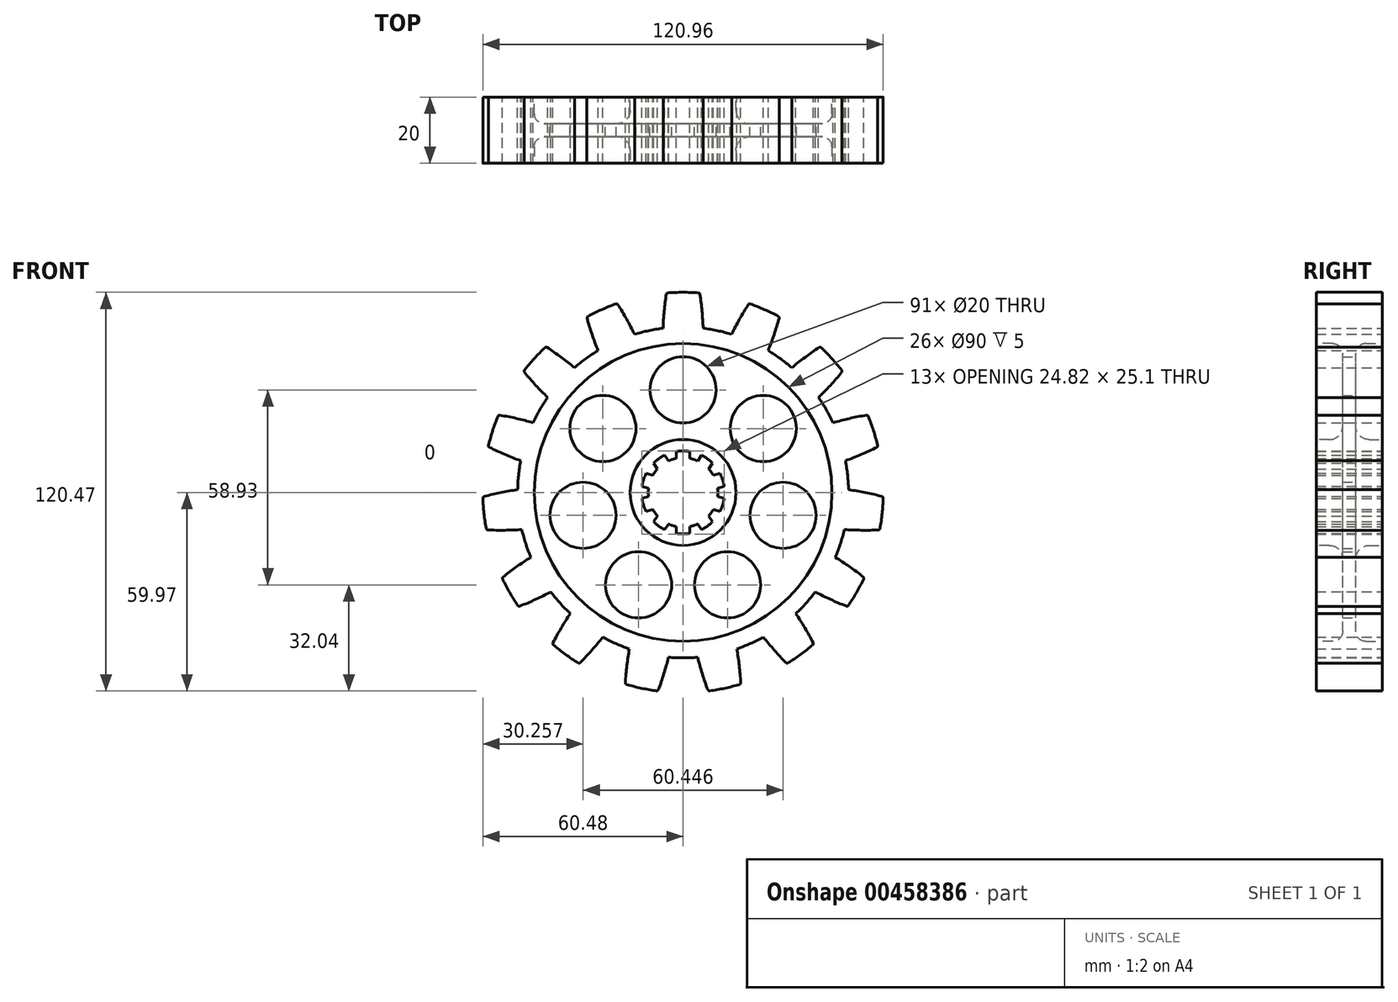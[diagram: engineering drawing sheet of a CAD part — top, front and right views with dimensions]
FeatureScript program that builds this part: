
annotation { "Feature Type Name" : "Feature", "Feature Type Description" : "" }
export const myFeature = defineFeature(function(context is Context, id is Id, definition is map)
    precondition{}
    {
        {
            var Q0;
            Q0=qCreatedBy(makeId("Front.planeOp"),FACE);
            var sketch = newSketch(context, id + "F0", { "sketchPlane" : qUnion([Q0])});
            skCircle(sketch, "E0", {"center": v(0, 0) * mm, "radius": 50 * mm});
            skArc(sketch, "E1", {"start": v(-60.49, -1.3) * mm, "mid": v(-60.17, -6.32) * mm, "end": v(-59.43, -11.31) * mm});
            skLineSegment(sketch, "E2.0", {"start": v(0, 46.5) * mm, "end": v(-83.9, 46.5) * mm, "construction": true});
            skLineSegment(sketch, "E3", {"start": v(0, 46.5) * mm, "end": v(83.9, 46.5) * mm, "construction": true});
            skArc(sketch, "E4.trimOffspring", {"start": v(-5.04, 60.29) * mm, "mid": v(-5.7, 54.98) * mm, "end": v(-6.05, 49.63) * mm});
            skArc(sketch, "E5.1.0", {"start": v(-29.12, 53.03) * mm, "mid": v(-27.57, 47.9) * mm, "end": v(-25.71, 42.88) * mm});
            skArc(sketch, "E5.1.1", {"start": v(-14.66, 47.8) * mm, "mid": v(-17.15, 52.54) * mm, "end": v(-19.92, 57.13) * mm});
            skArc(sketch, "E5.2.1", {"start": v(-32.84, 37.7) * mm, "mid": v(-37.04, 41.02) * mm, "end": v(-41.43, 44.09) * mm});
            skArc(sketch, "E5.3.0", {"start": v(-58.9, 13.84) * mm, "mid": v(-54.05, 11.57) * mm, "end": v(-49.07, 9.59) * mm});
            skArc(sketch, "E5.3.1", {"start": v(-45.34, 21.09) * mm, "mid": v(-50.52, 22.4) * mm, "end": v(-55.78, 23.42) * mm});
            skArc(sketch, "E5.4.0", {"start": v(-59.43, -11.31) * mm, "mid": v(-54.08, -11.42) * mm, "end": v(-48.73, -11.2) * mm});
            skArc(sketch, "E5.4.1", {"start": v(-50, 0.82) * mm, "mid": v(-55.27, -0.08) * mm, "end": v(-60.49, -1.3) * mm});
            skArc(sketch, "E5.5.0", {"start": v(-49.7, -34.5) * mm, "mid": v(-44.76, -32.42) * mm, "end": v(-39.96, -30.05) * mm});
            skArc(sketch, "E5.5.1", {"start": v(-46, -19.58) * mm, "mid": v(-50.46, -22.55) * mm, "end": v(-54.73, -25.78) * mm});
            skArc(sketch, "E5.6.0", {"start": v(-31.36, -51.74) * mm, "mid": v(-27.7, -47.83) * mm, "end": v(-24.28, -43.7) * mm});
            skArc(sketch, "E5.6.1", {"start": v(-34.06, -36.6) * mm, "mid": v(-36.93, -41.13) * mm, "end": v(-39.51, -45.81) * mm});
            skArc(sketch, "E5.7.0", {"start": v(-7.6, -60.02) * mm, "mid": v(-5.85, -54.96) * mm, "end": v(-4.4, -49.8) * mm});
            skArc(sketch, "E5.7.1", {"start": v(-16.23, -47.3) * mm, "mid": v(-17, -52.6) * mm, "end": v(-17.46, -57.93) * mm});
            skArc(sketch, "E5.8.0", {"start": v(17.46, -57.93) * mm, "mid": v(17, -52.6) * mm, "end": v(16.23, -47.3) * mm});
            skArc(sketch, "E5.8.1", {"start": v(4.4, -49.8) * mm, "mid": v(5.85, -54.96) * mm, "end": v(7.6, -60.02) * mm});
            skArc(sketch, "E5.9.0", {"start": v(39.51, -45.81) * mm, "mid": v(36.93, -41.13) * mm, "end": v(34.06, -36.6) * mm});
            skArc(sketch, "E5.9.1", {"start": v(24.28, -43.7) * mm, "mid": v(27.7, -47.83) * mm, "end": v(31.36, -51.74) * mm});
            skArc(sketch, "E5.10.0", {"start": v(54.73, -25.78) * mm, "mid": v(50.46, -22.55) * mm, "end": v(46, -19.58) * mm});
            skArc(sketch, "E5.10.1", {"start": v(39.96, -30.05) * mm, "mid": v(44.76, -32.42) * mm, "end": v(49.7, -34.5) * mm});
            skArc(sketch, "E5.11.0", {"start": v(60.49, -1.3) * mm, "mid": v(55.27, -0.08) * mm, "end": v(50, 0.82) * mm});
            skArc(sketch, "E5.11.1", {"start": v(48.73, -11.2) * mm, "mid": v(54.08, -11.42) * mm, "end": v(59.43, -11.31) * mm});
            skArc(sketch, "E5.12.0", {"start": v(55.78, 23.42) * mm, "mid": v(50.52, 22.4) * mm, "end": v(45.34, 21.09) * mm});
            skArc(sketch, "E5.12.1", {"start": v(49.07, 9.59) * mm, "mid": v(54.05, 11.57) * mm, "end": v(58.9, 13.84) * mm});
            skArc(sketch, "E5.13.0", {"start": v(41.43, 44.09) * mm, "mid": v(37.04, 41.02) * mm, "end": v(32.84, 37.7) * mm});
            skArc(sketch, "E5.13.1", {"start": v(40.93, 28.72) * mm, "mid": v(44.67, 32.55) * mm, "end": v(48.17, 36.6) * mm});
            skArc(sketch, "E5.14.0", {"start": v(19.92, 57.13) * mm, "mid": v(17.15, 52.54) * mm, "end": v(14.66, 47.8) * mm});
            skArc(sketch, "E5.14.1", {"start": v(25.71, 42.88) * mm, "mid": v(27.57, 47.9) * mm, "end": v(29.12, 53.03) * mm});
            skArc(sketch, "E6.trimOffspring", {"start": v(6.05, 49.63) * mm, "mid": v(5.7, 54.98) * mm, "end": v(5.04, 60.29) * mm});
            skArc(sketch, "E7.trimOffspring", {"start": v(-48.17, 36.6) * mm, "mid": v(-44.67, 32.55) * mm, "end": v(-40.93, 28.72) * mm});
            skCircle(sketch, "E8", {"center": v(0, 0) * mm, "radius": 10.5 * mm});
            skArc(sketch, "E9", {"start": v(8.94, 8.81) * mm, "mid": v(7.38, 10.15) * mm, "end": v(5.62, 11.22) * mm});
            skLineSegment(sketch, "E10.0", {"start": v(-2.05, -10.3) * mm, "end": v(-2.05, 12.38) * mm});
            skLineSegment(sketch, "E11.2.1", {"start": v(11.14, -5.78) * mm, "end": v(-12.4, 1.88) * mm});
            skLineSegment(sketch, "E11.4.1", {"start": v(8.94, 8.81) * mm, "end": v(-5.62, -11.22) * mm});
            skLineSegment(sketch, "E11.4.2", {"start": v(4.4, 9.54) * mm, "end": v(-8.94, -8.81) * mm});
            skLineSegment(sketch, "E11.5.2", {"start": v(-2.05, 12.38) * mm, "end": v(-2.05, -12.38) * mm});
            skLineSegment(sketch, "E11.6.2", {"start": v(-8.94, 8.81) * mm, "end": v(5.62, -11.22) * mm});
            skLineSegment(sketch, "E12.trimOffspring", {"start": v(-5.62, 11.22) * mm, "end": v(8.94, -8.81) * mm});
            skLineSegment(sketch, "E13.trimOffspring", {"start": v(2.05, 12.38) * mm, "end": v(2.05, -12.38) * mm});
            skLineSegment(sketch, "E14.trimOffspring", {"start": v(-11.14, 5.78) * mm, "end": v(12.4, -1.88) * mm});
            skLineSegment(sketch, "E15.trimOffspring", {"start": v(-12.4, 1.88) * mm, "end": v(11.14, -5.78) * mm});
            skLineSegment(sketch, "E16.trimOffspring", {"start": v(12.4, 1.88) * mm, "end": v(-11.14, -5.78) * mm});
            skLineSegment(sketch, "E17.trimOffspring", {"start": v(11.14, 5.78) * mm, "end": v(-12.4, -1.88) * mm});
            skLineSegment(sketch, "E18.trimOffspring", {"start": v(12.4, -1.88) * mm, "end": v(-11.14, 5.78) * mm});
            skLineSegment(sketch, "E19.trimOffspring", {"start": v(8.94, -8.81) * mm, "end": v(-5.62, 11.22) * mm});
            skLineSegment(sketch, "E20.trimOffspring", {"start": v(5.62, -11.22) * mm, "end": v(-8.94, 8.81) * mm});
            skLineSegment(sketch, "E21.trimOffspring", {"start": v(2.05, -12.38) * mm, "end": v(2.05, 12.38) * mm});
            skLineSegment(sketch, "E22.trimOffspring", {"start": v(-5.62, -11.22) * mm, "end": v(8.94, 8.81) * mm});
            skLineSegment(sketch, "E23.trimOffspring", {"start": v(-8.94, -8.81) * mm, "end": v(5.62, 11.22) * mm});
            skLineSegment(sketch, "E24.trimOffspring", {"start": v(-12.4, -1.88) * mm, "end": v(9.16, 5.13) * mm});
            skLineSegment(sketch, "E25.trimOffspring", {"start": v(-11.14, -5.78) * mm, "end": v(12.4, 1.88) * mm});
            skArc(sketch, "E26.trimOffspring", {"start": v(12.4, 1.88) * mm, "mid": v(11.94, 3.88) * mm, "end": v(11.14, 5.78) * mm});
            skArc(sketch, "E27.trimOffspring", {"start": v(11.14, -5.78) * mm, "mid": v(11.94, -3.88) * mm, "end": v(12.4, -1.88) * mm});
            skArc(sketch, "E28.trimOffspring", {"start": v(5.62, -11.22) * mm, "mid": v(7.38, -10.15) * mm, "end": v(8.94, -8.81) * mm});
            skArc(sketch, "E29.trimOffspring", {"start": v(-2.05, -12.38) * mm, "mid": v(0, -12.55) * mm, "end": v(2.05, -12.38) * mm});
            skArc(sketch, "E30.trimOffspring", {"start": v(-8.94, -8.81) * mm, "mid": v(-7.38, -10.15) * mm, "end": v(-5.62, -11.22) * mm});
            skArc(sketch, "E31.trimOffspring", {"start": v(-12.4, -1.88) * mm, "mid": v(-11.94, -3.88) * mm, "end": v(-11.14, -5.78) * mm});
            skArc(sketch, "E32.trimOffspring", {"start": v(-11.14, 5.78) * mm, "mid": v(-11.94, 3.88) * mm, "end": v(-12.4, 1.88) * mm});
            skArc(sketch, "E33.trimOffspring", {"start": v(-5.62, 11.22) * mm, "mid": v(-7.38, 10.15) * mm, "end": v(-8.94, 8.81) * mm});
            skArc(sketch, "E34.trimOffspring", {"start": v(2.05, 12.38) * mm, "mid": v(0, 12.55) * mm, "end": v(-2.05, 12.38) * mm});
            skArc(sketch, "E35.trimOffspring", {"start": v(-55.78, 23.42) * mm, "mid": v(-57.54, 18.7) * mm, "end": v(-58.9, 13.84) * mm});
            skArc(sketch, "E36.trimOffspring", {"start": v(-41.43, 44.09) * mm, "mid": v(-44.96, 40.48) * mm, "end": v(-48.17, 36.6) * mm});
            skArc(sketch, "E37.trimOffspring", {"start": v(-19.92, 57.13) * mm, "mid": v(-24.6, 55.27) * mm, "end": v(-29.12, 53.03) * mm});
            skArc(sketch, "E38.trimOffspring", {"start": v(5.04, 60.29) * mm, "mid": v(0, 60.5) * mm, "end": v(-5.04, 60.29) * mm});
            skArc(sketch, "E39.trimOffspring", {"start": v(29.12, 53.03) * mm, "mid": v(24.6, 55.27) * mm, "end": v(19.92, 57.13) * mm});
            skArc(sketch, "E40.trimOffspring", {"start": v(48.17, 36.6) * mm, "mid": v(44.96, 40.48) * mm, "end": v(41.43, 44.09) * mm});
            skArc(sketch, "E41.trimOffspring", {"start": v(58.9, 13.84) * mm, "mid": v(57.54, 18.7) * mm, "end": v(55.78, 23.42) * mm});
            skArc(sketch, "E42.trimOffspring", {"start": v(59.43, -11.31) * mm, "mid": v(60.17, -6.32) * mm, "end": v(60.49, -1.3) * mm});
            skArc(sketch, "E43.trimOffspring", {"start": v(49.7, -34.5) * mm, "mid": v(52.4, -30.25) * mm, "end": v(54.73, -25.78) * mm});
            skArc(sketch, "E44.trimOffspring", {"start": v(31.36, -51.74) * mm, "mid": v(35.56, -48.95) * mm, "end": v(39.51, -45.81) * mm});
            skArc(sketch, "E45.trimOffspring", {"start": v(7.6, -60.02) * mm, "mid": v(12.58, -59.18) * mm, "end": v(17.46, -57.93) * mm});
            skArc(sketch, "E46.trimOffspring", {"start": v(-17.46, -57.93) * mm, "mid": v(-12.58, -59.18) * mm, "end": v(-7.6, -60.02) * mm});
            skArc(sketch, "E47.trimOffspring", {"start": v(-39.51, -45.81) * mm, "mid": v(-35.56, -48.95) * mm, "end": v(-31.36, -51.74) * mm});
            skArc(sketch, "E48.trimOffspring", {"start": v(-54.73, -25.78) * mm, "mid": v(-52.4, -30.25) * mm, "end": v(-49.7, -34.5) * mm});
            skSolve(sketch);
        }
        {
            var Q0;
            {var subQ9=sQuery(id+"F0.wireOp",EDGE,"E9");Q0=makeQuery(id+"F0.imprint","IMPRINT",FACE,{"disambiguationData":[TD([[makeQuery(id+"F0.imprint","IMPRINT",EDGE,{"derivedFrom":subQ9}),-1.0]])]});}
            var Q1;
            Q1=makeQuery(id+"F0.imprint","IMPRINT",FACE,{"disambiguationData":[TD([[makeQuery(id+"F0.imprint","IMPRINT",EDGE,{"derivedFrom":sQuery(id+"F0.wireOp",EDGE,"E1")}),1.0]])]});
            var Q2;
            {var subQ0=sQuery(id+"F0.wireOp",EDGE,"E5.3.0");Q2=makeQuery(id+"F0.imprint","IMPRINT",FACE,{"disambiguationData":[TD([[makeQuery(id+"F0.imprint","IMPRINT",EDGE,{"derivedFrom":subQ0}),1.0]])]});}
            var Q3;
            {var subQ0=sQuery(id+"F0.wireOp",EDGE,"E5.2.1");Q3=makeQuery(id+"F0.imprint","IMPRINT",FACE,{"disambiguationData":[TD([[makeQuery(id+"F0.imprint","IMPRINT",EDGE,{"derivedFrom":subQ0}),1.0]])]});}
            var Q4;
            {var subQ0=sQuery(id+"F0.wireOp",EDGE,"E5.1.0");Q4=makeQuery(id+"F0.imprint","IMPRINT",FACE,{"disambiguationData":[TD([[makeQuery(id+"F0.imprint","IMPRINT",EDGE,{"derivedFrom":subQ0}),1.0]])]});}
            var Q5;
            {var subQ0=sQuery(id+"F0.wireOp",EDGE,"E4.trimOffspring");Q5=makeQuery(id+"F0.imprint","IMPRINT",FACE,{"disambiguationData":[TD([[makeQuery(id+"F0.imprint","IMPRINT",EDGE,{"derivedFrom":subQ0}),1.0]])]});}
            var Q6;
            {var subQ0=sQuery(id+"F0.wireOp",EDGE,"E5.14.0");Q6=makeQuery(id+"F0.imprint","IMPRINT",FACE,{"disambiguationData":[TD([[makeQuery(id+"F0.imprint","IMPRINT",EDGE,{"derivedFrom":subQ0}),1.0]])]});}
            var Q7;
            {var subQ0=sQuery(id+"F0.wireOp",EDGE,"E5.13.0");Q7=makeQuery(id+"F0.imprint","IMPRINT",FACE,{"disambiguationData":[TD([[makeQuery(id+"F0.imprint","IMPRINT",EDGE,{"derivedFrom":subQ0}),1.0]])]});}
            var Q8;
            {var subQ0=sQuery(id+"F0.wireOp",EDGE,"E5.12.0");Q8=makeQuery(id+"F0.imprint","IMPRINT",FACE,{"disambiguationData":[TD([[makeQuery(id+"F0.imprint","IMPRINT",EDGE,{"derivedFrom":subQ0}),1.0]])]});}
            var Q9;
            {var subQ0=sQuery(id+"F0.wireOp",EDGE,"E5.11.0");Q9=makeQuery(id+"F0.imprint","IMPRINT",FACE,{"disambiguationData":[TD([[makeQuery(id+"F0.imprint","IMPRINT",EDGE,{"derivedFrom":subQ0}),1.0]])]});}
            var Q10;
            {var subQ0=sQuery(id+"F0.wireOp",EDGE,"E5.10.0");Q10=makeQuery(id+"F0.imprint","IMPRINT",FACE,{"disambiguationData":[TD([[makeQuery(id+"F0.imprint","IMPRINT",EDGE,{"derivedFrom":subQ0}),1.0]])]});}
            var Q11;
            {var subQ0=sQuery(id+"F0.wireOp",EDGE,"E5.9.0");Q11=makeQuery(id+"F0.imprint","IMPRINT",FACE,{"disambiguationData":[TD([[makeQuery(id+"F0.imprint","IMPRINT",EDGE,{"derivedFrom":subQ0}),1.0]])]});}
            var Q12;
            {var subQ0=sQuery(id+"F0.wireOp",EDGE,"E5.8.0");Q12=makeQuery(id+"F0.imprint","IMPRINT",FACE,{"disambiguationData":[TD([[makeQuery(id+"F0.imprint","IMPRINT",EDGE,{"derivedFrom":subQ0}),1.0]])]});}
            var Q13;
            {var subQ0=sQuery(id+"F0.wireOp",EDGE,"E5.7.0");Q13=makeQuery(id+"F0.imprint","IMPRINT",FACE,{"disambiguationData":[TD([[makeQuery(id+"F0.imprint","IMPRINT",EDGE,{"derivedFrom":subQ0}),1.0]])]});}
            var Q14;
            {var subQ0=sQuery(id+"F0.wireOp",EDGE,"E5.6.0");Q14=makeQuery(id+"F0.imprint","IMPRINT",FACE,{"disambiguationData":[TD([[makeQuery(id+"F0.imprint","IMPRINT",EDGE,{"derivedFrom":subQ0}),1.0]])]});}
            var Q15;
            {var subQ0=sQuery(id+"F0.wireOp",EDGE,"E5.5.0");Q15=makeQuery(id+"F0.imprint","IMPRINT",FACE,{"disambiguationData":[TD([[makeQuery(id+"F0.imprint","IMPRINT",EDGE,{"derivedFrom":subQ0}),1.0]])]});}
            extrude(context, id + "F1", {"entities" : qUnion([Q0, Q1, Q2, Q3, Q4, Q5, Q6, Q7, Q8, Q9, Q10, Q11, Q12, Q13, Q14, Q15]), "depth" : 20 * mm, "offsetDistance" : 25 * mm});
        }
        {
            var Q0;
            Q0=qCreatedBy(makeId("Front.planeOp"),FACE);
            var sketch = newSketch(context, id + "F2", { "sketchPlane" : qUnion([Q0])});
            skCircle(sketch, "E49", {"center": v(0, 31) * mm, "radius": 10 * mm});
            skCircle(sketch, "E50.1.0", {"center": v(-24.24, 19.33) * mm, "radius": 10 * mm});
            skCircle(sketch, "E50.2.0", {"center": v(-30.22, -6.9) * mm, "radius": 10 * mm});
            skCircle(sketch, "E50.3.0", {"center": v(-13.45, -27.93) * mm, "radius": 10 * mm});
            skCircle(sketch, "E50.4.0", {"center": v(13.45, -27.93) * mm, "radius": 10 * mm});
            skCircle(sketch, "E50.5.0", {"center": v(30.22, -6.9) * mm, "radius": 10 * mm});
            skCircle(sketch, "E50.6.0", {"center": v(24.24, 19.33) * mm, "radius": 10 * mm});
            skPoint(sketch, "E50.center", {"position": v(0, 0) * mm});
            skSolve(sketch);
        }
        {
            var Q0;
            Q0 = qSketchRegion(id + "F2", true);
            extrude(context, id + "F3", {"entities" : qUnion([Q0]), "operationType" : NewBodyOperationType.REMOVE, "depth" : 56 * mm, "offsetDistance" : 25 * mm});
        }
        {
            var Q0;
            Q0=qCreatedBy(makeId("Front.planeOp"),FACE);
            cPlane(context, id + "F4", {"entities" : qUnion([Q0]), "cplaneType" : CPlaneType.OFFSET, "offset" : 20 * mm, "width" : 150 * mm, "height" : 150 * mm});
        }
        {
            var Q0;
            Q0=qCreatedBy(id+"F4.planeOp",FACE);
            var sketch = newSketch(context, id + "F5", { "sketchPlane" : qUnion([Q0])});
            skCircle(sketch, "E51", {"center": v(0, 0) * mm, "radius": 16 * mm});
            skCircle(sketch, "E52", {"center": v(0, 0) * mm, "radius": 45 * mm});
            skSolve(sketch);
        }
        {
            var Q0;
            Q0=makeQuery(id+"F5.imprint","IMPRINT",FACE,{"disambiguationData":[TD([[makeQuery(id+"F5.imprint","IMPRINT",EDGE,{"derivedFrom":sQuery(id+"F5.wireOp",EDGE,"E51")}),-1.0]])]});
            extrude(context, id + "F6", {"entities" : qUnion([Q0]), "operationType" : NewBodyOperationType.REMOVE, "oppositeDirection" : true, "depth" : 8 * mm, "offsetDistance" : 25 * mm});
        }
        {
            var Q0;
            Q0=qCreatedBy(makeId("Front.planeOp"),FACE);
            var sketch = newSketch(context, id + "F7", { "sketchPlane" : qUnion([Q0])});
            skCircle(sketch, "E53", {"center": v(0, 0) * mm, "radius": 16 * mm});
            skCircle(sketch, "E54", {"center": v(0, 0) * mm, "radius": 45 * mm});
            skSolve(sketch);
        }
        {
            var Q0;
            Q0=makeQuery(id+"F7.imprint","IMPRINT",FACE,{"disambiguationData":[TD([[makeQuery(id+"F7.imprint","IMPRINT",EDGE,{"derivedFrom":sQuery(id+"F7.wireOp",EDGE,"E53")}),-1.0]])]});
            extrude(context, id + "F8", {"entities" : qUnion([Q0]), "operationType" : NewBodyOperationType.REMOVE, "depth" : 8 * mm, "offsetDistance" : 25 * mm});
        }
        {
            var Q0;
            Q0=makeQuery(id+"F6.boolean.opBoolean","COPY",EDGE,{"derivedFrom":makeQuery(id+"F6.opExtrude","CAP_EDGE",EDGE,{"disambiguationData":[OSD([sQuery(id+"F5.wireOp",EDGE,"E52")])],"isStart":false})});
            var Q1;
            Q1=makeQuery(id+"F8.boolean.opBoolean","COPY",EDGE,{"derivedFrom":makeQuery(id+"F8.opExtrude","CAP_EDGE",EDGE,{"disambiguationData":[OSD([sQuery(id+"F7.wireOp",EDGE,"E54")])],"isStart":false})});
            fillet(context, id + "F9", {"entities" : qUnion([Q0, Q1]), "radius" : 3 * mm, "tangentPropagation" : true, "allowEdgeOverflow" : false});
        }
        {
            var Q0;
            Q0=makeQuery(id+"F6.boolean.opBoolean","COPY",EDGE,{"derivedFrom":makeQuery(id+"F6.opExtrude","CAP_EDGE",EDGE,{"disambiguationData":[OSD([sQuery(id+"F5.wireOp",EDGE,"E51")])],"isStart":false})});
            var Q1;
            Q1=makeQuery(id+"F8.boolean.opBoolean","COPY",EDGE,{"derivedFrom":makeQuery(id+"F8.opExtrude","CAP_EDGE",EDGE,{"disambiguationData":[OSD([sQuery(id+"F7.wireOp",EDGE,"E53")])],"isStart":false})});
            fillet(context, id + "F10", {"entities" : qUnion([Q0, Q1]), "radius" : 4 * mm, "tangentPropagation" : true, "allowEdgeOverflow" : false});
        }
        {
            var Q0;
            Q0=makeQuery(id+"F1.opExtrude","SWEPT_EDGE",EDGE,{"disambiguationData":[OSD([sQuery(id+"F0.wireOp",EDGE,"E6.trimOffspring"),sQuery(id+"F0.wireOp",EDGE,"E38.trimOffspring")])]});
            var Q1;
            Q1=makeQuery(id+"F1.opExtrude","SWEPT_EDGE",EDGE,{"disambiguationData":[OSD([sQuery(id+"F0.wireOp",EDGE,"E4.trimOffspring"),sQuery(id+"F0.wireOp",EDGE,"E38.trimOffspring")])]});
            var Q2;
            Q2=makeQuery(id+"F1.opExtrude","SWEPT_EDGE",EDGE,{"disambiguationData":[OSD([sQuery(id+"F0.wireOp",EDGE,"E5.14.1"),sQuery(id+"F0.wireOp",EDGE,"E39.trimOffspring")])]});
            var Q3;
            Q3=makeQuery(id+"F1.opExtrude","SWEPT_EDGE",EDGE,{"disambiguationData":[OSD([sQuery(id+"F0.wireOp",EDGE,"E5.14.0"),sQuery(id+"F0.wireOp",EDGE,"E39.trimOffspring")])]});
            var Q4;
            Q4=makeQuery(id+"F1.opExtrude","SWEPT_EDGE",EDGE,{"disambiguationData":[OSD([sQuery(id+"F0.wireOp",EDGE,"E5.1.0"),sQuery(id+"F0.wireOp",EDGE,"E37.trimOffspring")])]});
            var Q5;
            Q5=makeQuery(id+"F1.opExtrude","SWEPT_EDGE",EDGE,{"disambiguationData":[OSD([sQuery(id+"F0.wireOp",EDGE,"E5.1.1"),sQuery(id+"F0.wireOp",EDGE,"E37.trimOffspring")])]});
            var Q6;
            Q6=makeQuery(id+"F1.opExtrude","SWEPT_EDGE",EDGE,{"disambiguationData":[OSD([sQuery(id+"F0.wireOp",EDGE,"E5.2.1"),sQuery(id+"F0.wireOp",EDGE,"E36.trimOffspring")])]});
            var Q7;
            Q7=makeQuery(id+"F1.opExtrude","SWEPT_EDGE",EDGE,{"disambiguationData":[OSD([sQuery(id+"F0.wireOp",EDGE,"E7.trimOffspring"),sQuery(id+"F0.wireOp",EDGE,"E36.trimOffspring")])]});
            var Q8;
            Q8=makeQuery(id+"F1.opExtrude","SWEPT_EDGE",EDGE,{"disambiguationData":[OSD([sQuery(id+"F0.wireOp",EDGE,"E5.3.1"),sQuery(id+"F0.wireOp",EDGE,"E35.trimOffspring")])]});
            var Q9;
            Q9=makeQuery(id+"F1.opExtrude","SWEPT_EDGE",EDGE,{"disambiguationData":[OSD([sQuery(id+"F0.wireOp",EDGE,"E5.3.0"),sQuery(id+"F0.wireOp",EDGE,"E35.trimOffspring")])]});
            var Q10;
            Q10=makeQuery(id+"F1.opExtrude","SWEPT_EDGE",EDGE,{"disambiguationData":[OSD([sQuery(id+"F0.wireOp",EDGE,"E1"),sQuery(id+"F0.wireOp",EDGE,"E5.4.1")])]});
            var Q11;
            Q11=makeQuery(id+"F1.opExtrude","SWEPT_EDGE",EDGE,{"disambiguationData":[OSD([sQuery(id+"F0.wireOp",EDGE,"E1"),sQuery(id+"F0.wireOp",EDGE,"E5.4.0")])]});
            var Q12;
            Q12=makeQuery(id+"F1.opExtrude","SWEPT_EDGE",EDGE,{"disambiguationData":[OSD([sQuery(id+"F0.wireOp",EDGE,"E5.5.1"),sQuery(id+"F0.wireOp",EDGE,"E48.trimOffspring")])]});
            var Q13;
            Q13=makeQuery(id+"F1.opExtrude","SWEPT_EDGE",EDGE,{"disambiguationData":[OSD([sQuery(id+"F0.wireOp",EDGE,"E5.5.0"),sQuery(id+"F0.wireOp",EDGE,"E48.trimOffspring")])]});
            var Q14;
            Q14=makeQuery(id+"F1.opExtrude","SWEPT_EDGE",EDGE,{"disambiguationData":[OSD([sQuery(id+"F0.wireOp",EDGE,"E5.6.1"),sQuery(id+"F0.wireOp",EDGE,"E47.trimOffspring")])]});
            var Q15;
            Q15=makeQuery(id+"F1.opExtrude","SWEPT_EDGE",EDGE,{"disambiguationData":[OSD([sQuery(id+"F0.wireOp",EDGE,"E5.6.0"),sQuery(id+"F0.wireOp",EDGE,"E47.trimOffspring")])]});
            var Q16;
            Q16=makeQuery(id+"F1.opExtrude","SWEPT_EDGE",EDGE,{"disambiguationData":[OSD([sQuery(id+"F0.wireOp",EDGE,"E5.7.1"),sQuery(id+"F0.wireOp",EDGE,"E46.trimOffspring")])]});
            var Q17;
            Q17=makeQuery(id+"F1.opExtrude","SWEPT_EDGE",EDGE,{"disambiguationData":[OSD([sQuery(id+"F0.wireOp",EDGE,"E5.7.0"),sQuery(id+"F0.wireOp",EDGE,"E46.trimOffspring")])]});
            var Q18;
            Q18=makeQuery(id+"F1.opExtrude","SWEPT_EDGE",EDGE,{"disambiguationData":[OSD([sQuery(id+"F0.wireOp",EDGE,"E5.8.1"),sQuery(id+"F0.wireOp",EDGE,"E45.trimOffspring")])]});
            var Q19;
            Q19=makeQuery(id+"F1.opExtrude","SWEPT_EDGE",EDGE,{"disambiguationData":[OSD([sQuery(id+"F0.wireOp",EDGE,"E5.8.0"),sQuery(id+"F0.wireOp",EDGE,"E45.trimOffspring")])]});
            var Q20;
            Q20=makeQuery(id+"F1.opExtrude","SWEPT_EDGE",EDGE,{"disambiguationData":[OSD([sQuery(id+"F0.wireOp",EDGE,"E5.9.1"),sQuery(id+"F0.wireOp",EDGE,"E44.trimOffspring")])]});
            var Q21;
            Q21=makeQuery(id+"F1.opExtrude","SWEPT_EDGE",EDGE,{"disambiguationData":[OSD([sQuery(id+"F0.wireOp",EDGE,"E5.9.0"),sQuery(id+"F0.wireOp",EDGE,"E44.trimOffspring")])]});
            var Q22;
            Q22=makeQuery(id+"F1.opExtrude","SWEPT_EDGE",EDGE,{"disambiguationData":[OSD([sQuery(id+"F0.wireOp",EDGE,"E5.10.1"),sQuery(id+"F0.wireOp",EDGE,"E43.trimOffspring")])]});
            var Q23;
            Q23=makeQuery(id+"F1.opExtrude","SWEPT_EDGE",EDGE,{"disambiguationData":[OSD([sQuery(id+"F0.wireOp",EDGE,"E5.10.0"),sQuery(id+"F0.wireOp",EDGE,"E43.trimOffspring")])]});
            var Q24;
            Q24=makeQuery(id+"F1.opExtrude","SWEPT_EDGE",EDGE,{"disambiguationData":[OSD([sQuery(id+"F0.wireOp",EDGE,"E5.11.1"),sQuery(id+"F0.wireOp",EDGE,"E42.trimOffspring")])]});
            var Q25;
            Q25=makeQuery(id+"F1.opExtrude","SWEPT_EDGE",EDGE,{"disambiguationData":[OSD([sQuery(id+"F0.wireOp",EDGE,"E5.11.0"),sQuery(id+"F0.wireOp",EDGE,"E42.trimOffspring")])]});
            var Q26;
            Q26=makeQuery(id+"F1.opExtrude","SWEPT_EDGE",EDGE,{"disambiguationData":[OSD([sQuery(id+"F0.wireOp",EDGE,"E5.13.0"),sQuery(id+"F0.wireOp",EDGE,"E40.trimOffspring")])]});
            var Q27;
            Q27=makeQuery(id+"F1.opExtrude","SWEPT_EDGE",EDGE,{"disambiguationData":[OSD([sQuery(id+"F0.wireOp",EDGE,"E5.13.1"),sQuery(id+"F0.wireOp",EDGE,"E40.trimOffspring")])]});
            var Q28;
            Q28=makeQuery(id+"F1.opExtrude","SWEPT_EDGE",EDGE,{"disambiguationData":[OSD([sQuery(id+"F0.wireOp",EDGE,"E5.12.0"),sQuery(id+"F0.wireOp",EDGE,"E41.trimOffspring")])]});
            var Q29;
            Q29=makeQuery(id+"F1.opExtrude","SWEPT_EDGE",EDGE,{"disambiguationData":[OSD([sQuery(id+"F0.wireOp",EDGE,"E5.12.1"),sQuery(id+"F0.wireOp",EDGE,"E41.trimOffspring")])]});
            fillet(context, id + "F11", {"entities" : qUnion([Q0, Q1, Q2, Q3, Q4, Q5, Q6, Q7, Q8, Q9, Q10, Q11, Q12, Q13, Q14, Q15, Q16, Q17, Q18, Q19, Q20, Q21, Q22, Q23, Q24, Q25, Q26, Q27, Q28, Q29]), "radius" : 0.5 * mm, "tangentPropagation" : true, "allowEdgeOverflow" : false});
        }
    });
